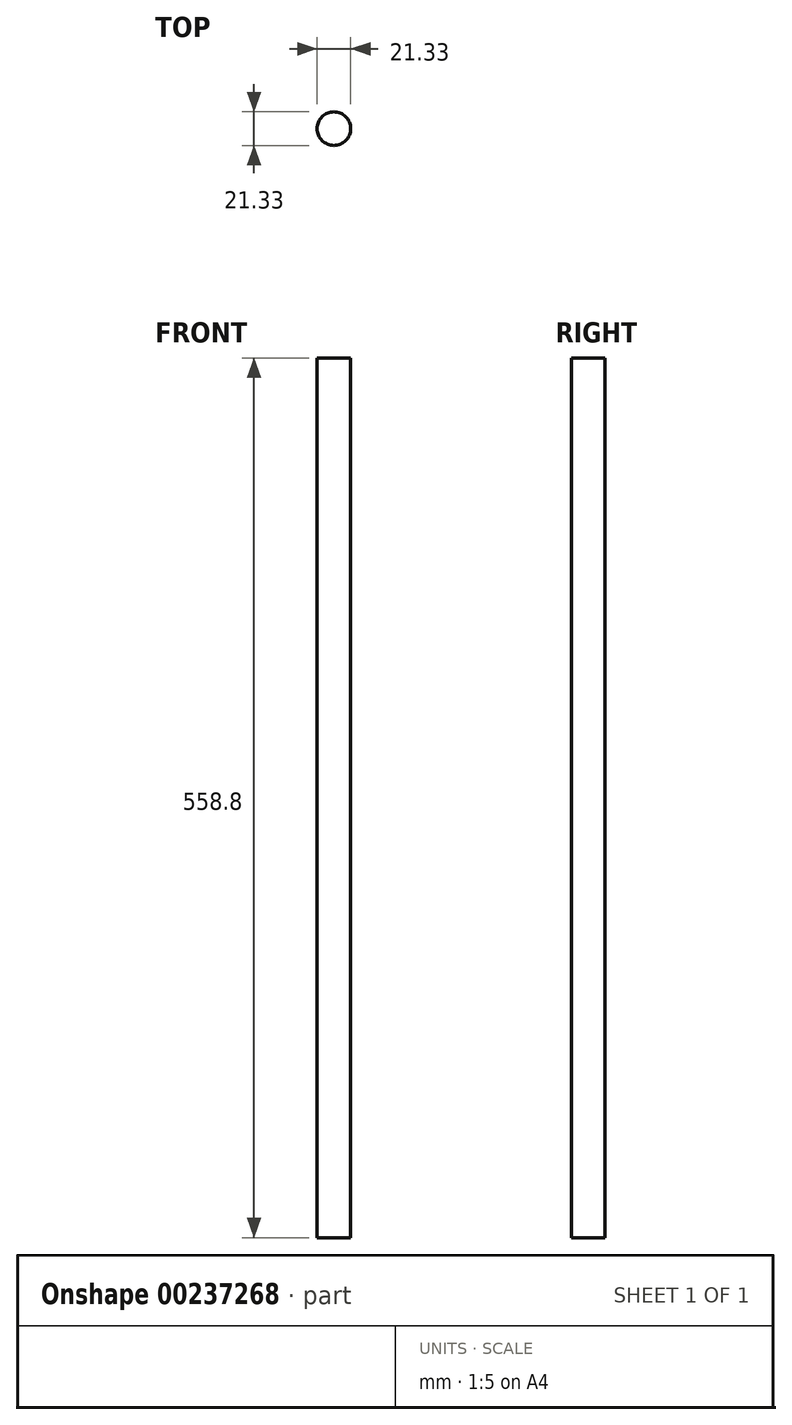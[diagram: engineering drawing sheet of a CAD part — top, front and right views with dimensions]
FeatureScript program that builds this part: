
annotation { "Feature Type Name" : "Feature", "Feature Type Description" : "" }
export const myFeature = defineFeature(function(context is Context, id is Id, definition is map)
    precondition{}
    {
        {
            var Q0;
            Q0=qCreatedBy(makeId("Top.planeOp"),FACE);
            var sketch = newSketch(context, id + "F0", { "sketchPlane" : qUnion([Q0])});
            skCircle(sketch, "E0", {"center": v(-14.96, 8.46) * mm, "radius": 10.67 * mm});
            skSolve(sketch);
        }
        {
            var Q0;
            Q0 = qSketchRegion(id + "F0", true);
            extrude(context, id + "F1", {"entities" : qUnion([Q0]), "depth" : 558.8 * mm});
        }
    });
